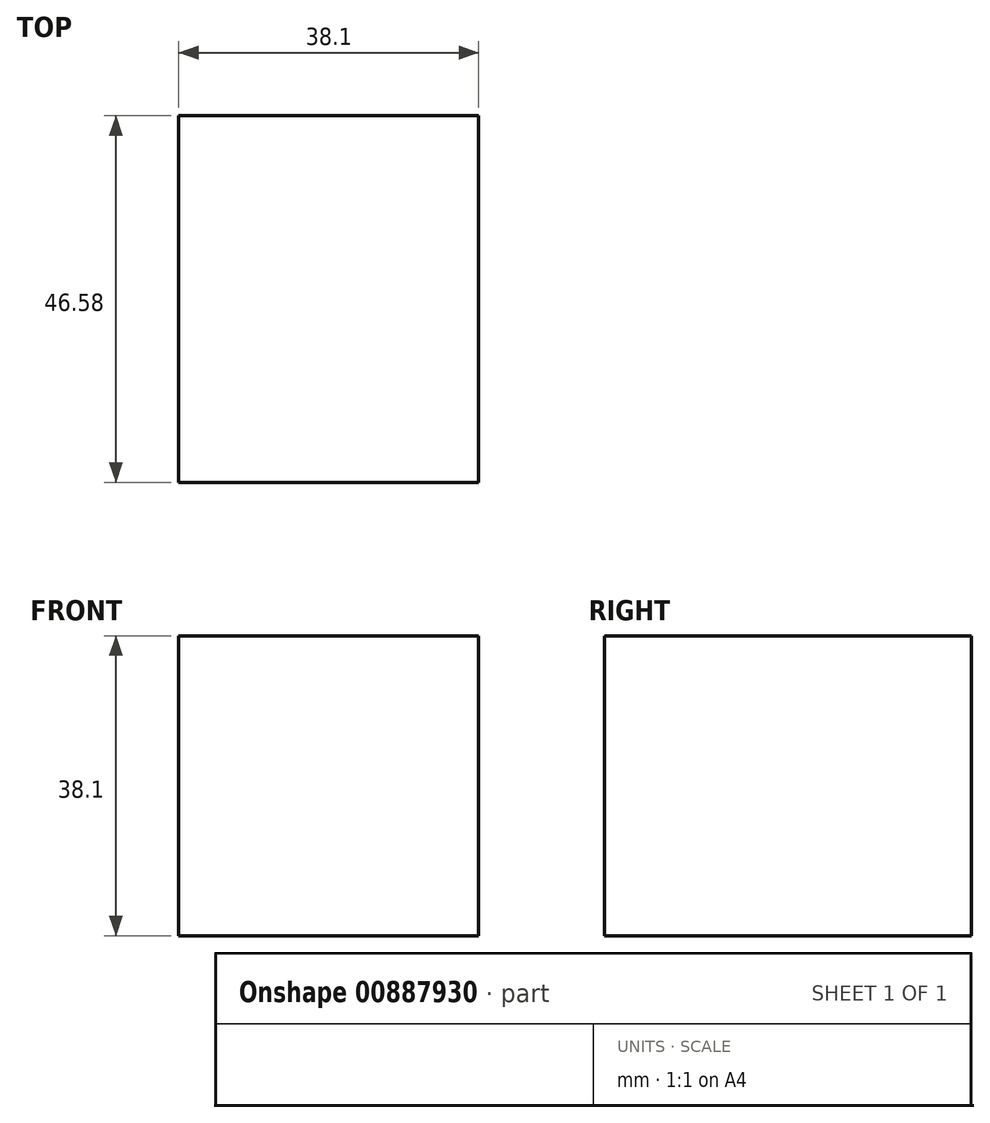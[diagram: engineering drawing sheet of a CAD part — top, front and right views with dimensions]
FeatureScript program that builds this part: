
annotation { "Feature Type Name" : "Feature", "Feature Type Description" : "" }
export const myFeature = defineFeature(function(context is Context, id is Id, definition is map)
    precondition{}
    {
        {
            assignVariable(context, id + "F0", {"name" : "WoodThickness", "anyValue" : .71});
        }
        {
            var Q0;
            Q0=qCreatedBy(makeId("Front.planeOp"),FACE);
            var sketch = newSketch(context, id + "F1", { "sketchPlane" : qUnion([Q0])});
            skLineSegment(sketch, "E0.bottom", {"start": v(19.05, 19.05) * mm, "end": v(-19.05, 19.05) * mm});
            skLineSegment(sketch, "E0.top", {"start": v(19.05, -19.05) * mm, "end": v(-19.05, -19.05) * mm});
            skLineSegment(sketch, "E0.left", {"start": v(19.05, 19.05) * mm, "end": v(19.05, -19.05) * mm});
            skLineSegment(sketch, "E0.right", {"start": v(-19.05, 19.05) * mm, "end": v(-19.05, -19.05) * mm});
            skPoint(sketch, "E0.middle", {"position": v(0, 0) * mm});
            skSolve(sketch);
        }
        {
            var Q0;
            Q0 = qSketchRegion(id + "F1", true);
            extrude(context, id + "F2", {"entities" : qUnion([Q0]), "depth" : (48 - (2 * getVariable(context, 'WoodThickness'))) * mm, "offsetDistance" : 25.4 * mm});
        }
    });
